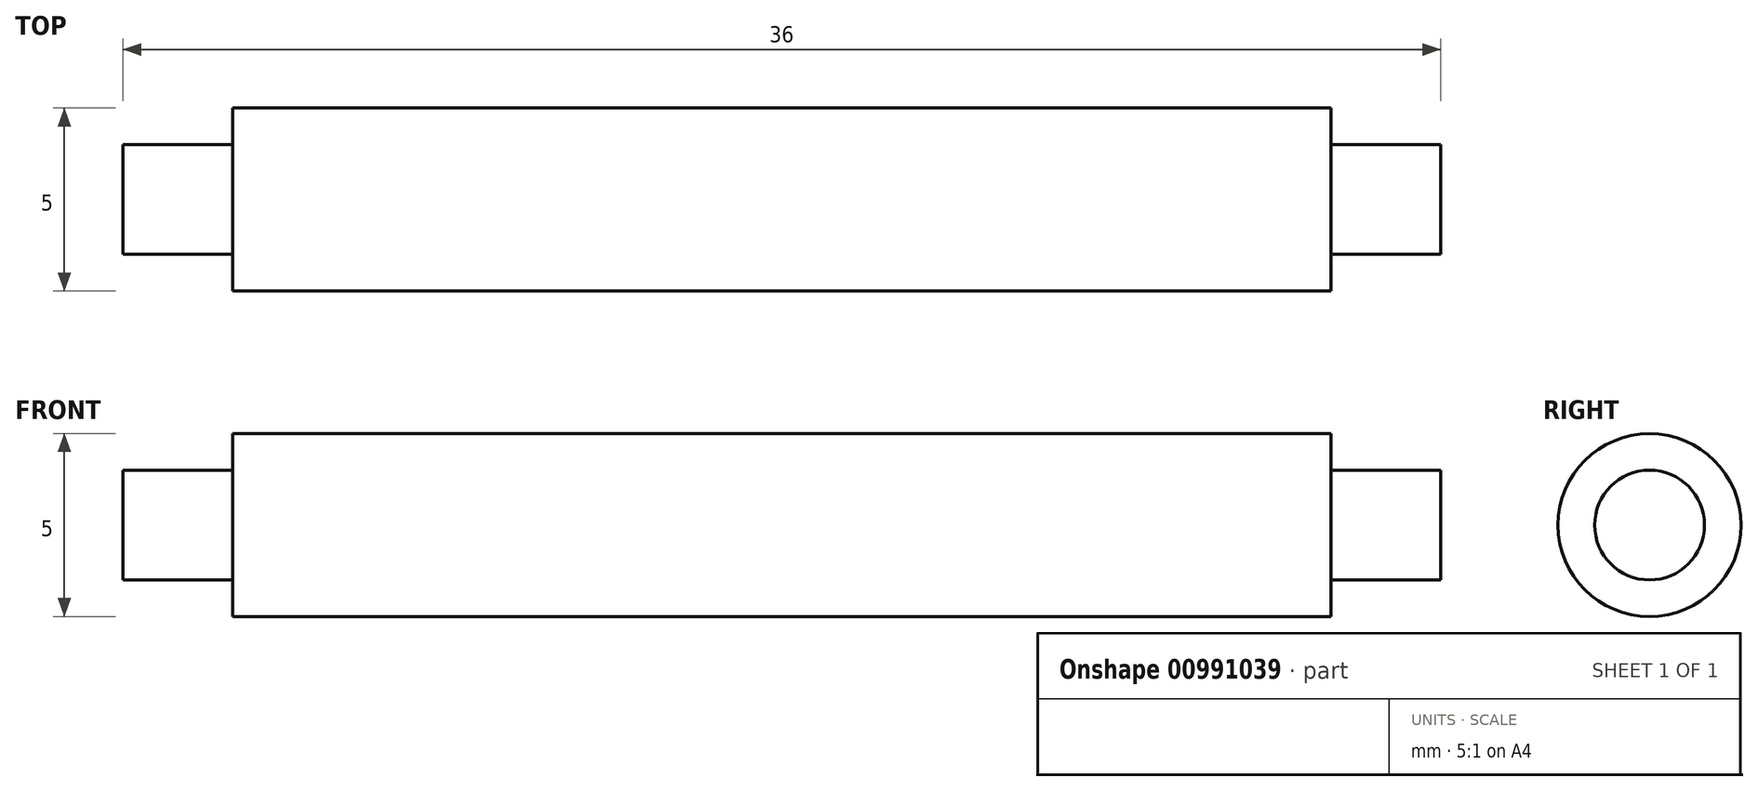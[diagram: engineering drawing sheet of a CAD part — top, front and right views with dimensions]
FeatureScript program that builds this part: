
annotation { "Feature Type Name" : "Feature", "Feature Type Description" : "" }
export const myFeature = defineFeature(function(context is Context, id is Id, definition is map)
    precondition{}
    {
        {
            var Q0;
            Q0=qCreatedBy(makeId("Top.planeOp"),FACE);
            var sketch = newSketch(context, id + "F0", { "sketchPlane" : qUnion([Q0])});
            skLineSegment(sketch, "E0", {"start": v(-23.83, 0) * mm, "end": v(24.61, 0) * mm, "construction": true});
            skLineSegment(sketch, "E1", {"start": v(-18, 0) * mm, "end": v(-18, 1.5) * mm});
            skLineSegment(sketch, "E2", {"start": v(-18, 1.5) * mm, "end": v(-15, 1.5) * mm});
            skLineSegment(sketch, "E3", {"start": v(-15, 1.5) * mm, "end": v(-15, 2.5) * mm});
            skLineSegment(sketch, "E4", {"start": v(-15, 2.5) * mm, "end": v(15, 2.5) * mm});
            skLineSegment(sketch, "E5", {"start": v(15, 2.5) * mm, "end": v(15, 1.5) * mm});
            skLineSegment(sketch, "E6", {"start": v(15, 1.5) * mm, "end": v(18, 1.5) * mm});
            skLineSegment(sketch, "E7", {"start": v(18, 1.5) * mm, "end": v(18, 0) * mm});
            skLineSegment(sketch, "E8", {"start": v(18, 0) * mm, "end": v(-18, 0) * mm});
            skSolve(sketch);
        }
        {
            var Q0;
            Q0=makeQuery(id+"F0.imprint","IMPRINT",FACE,{"disambiguationData":[TD([[makeQuery(id+"F0.imprint","IMPRINT",EDGE,{"derivedFrom":sQuery(id+"F0.wireOp",EDGE,"E1")}),-1.0]])]});
            var Q1;
            Q1=sQuery(id+"F0.wireOp",EDGE,"E8");
            revolve(context, id + "F1", {"surfaceOperationType" : NewSurfaceOperationType.NEW, "entities" : qUnion([Q0]), "axis" : qUnion([Q1]), "revolveType" : RevolveType.FULL});
        }
    });
